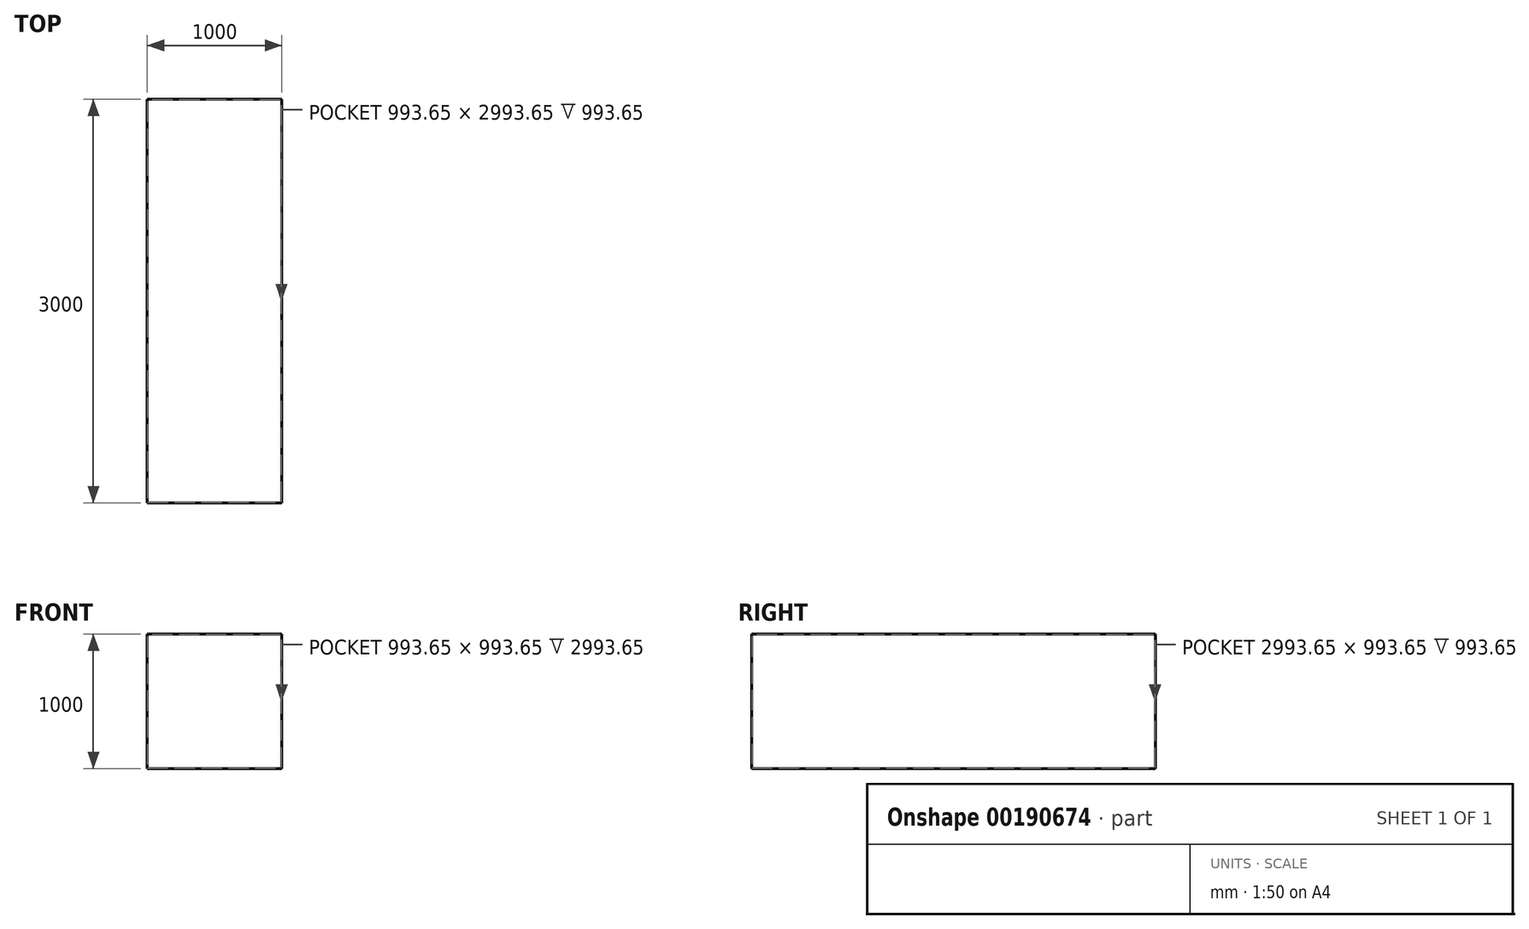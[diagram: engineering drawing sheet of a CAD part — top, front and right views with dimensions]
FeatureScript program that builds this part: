
annotation { "Feature Type Name" : "Feature", "Feature Type Description" : "" }
export const myFeature = defineFeature(function(context is Context, id is Id, definition is map)
    precondition{}
    {
        {
            var Q0;
            Q0=qCreatedBy(makeId("Front.planeOp"),FACE);
            var sketch = newSketch(context, id + "F0", { "sketchPlane" : qUnion([Q0])});
            skLineSegment(sketch, "E0.bottom", {"start": v(0, 0) * mm, "end": v(1000, 0) * mm});
            skLineSegment(sketch, "E0.top", {"start": v(0, 1000) * mm, "end": v(1000, 1000) * mm});
            skLineSegment(sketch, "E0.left", {"start": v(0, 0) * mm, "end": v(0, 1000) * mm});
            skLineSegment(sketch, "E0.right", {"start": v(1000, 0) * mm, "end": v(1000, 1000) * mm});
            skSolve(sketch);
        }
        {
            var Q0;
            Q0 = qSketchRegion(id + "F0", true);
            extrude(context, id + "F1", {"entities" : qUnion([Q0]), "depth" : 3000 / 2 * mm});
        }
        {
            var Q0;
            Q0=makeQuery(id+"F1.opExtrude","CAP_FACE",FACE,{"disambiguationData":[OSD([sQuery(id+"F0.wireOp",EDGE,"E0.bottom"),sQuery(id+"F0.wireOp",EDGE,"E0.top"),sQuery(id+"F0.wireOp",EDGE,"E0.left"),sQuery(id+"F0.wireOp",EDGE,"E0.right")])],"isStart":false});
            shell(context, id + "F2", {"entities" : qUnion([Q0]), "thickness" : 3.17 * mm});
        }
        {
            var Q0;
            Q0=qCreatedBy(makeId("Front.planeOp"),FACE);
            cPlane(context, id + "F3", {"entities" : qUnion([Q0]), "cplaneType" : CPlaneType.OFFSET, "offset" : 1500 * mm, "width" : 150 * mm, "height" : 150 * mm});
        }
        {
            var Q0;
            Q0=makeQuery(id+"F1.opExtrude","SWEPT_BODY",BODY,{"disambiguationData":[OSD([sQuery(id+"F0.wireOp",EDGE,"E0.bottom"),sQuery(id+"F0.wireOp",EDGE,"E0.top"),sQuery(id+"F0.wireOp",EDGE,"E0.left"),sQuery(id+"F0.wireOp",EDGE,"E0.right")])]});
            var Q1;
            Q1=qCreatedBy(id+"F3.planeOp",FACE);
            mirror(context, id + "F4", {"operationType" : NewBodyOperationType.ADD, "entities" : qUnion([Q0]), "mirrorPlane" : qUnion([Q1])});
        }
    });
